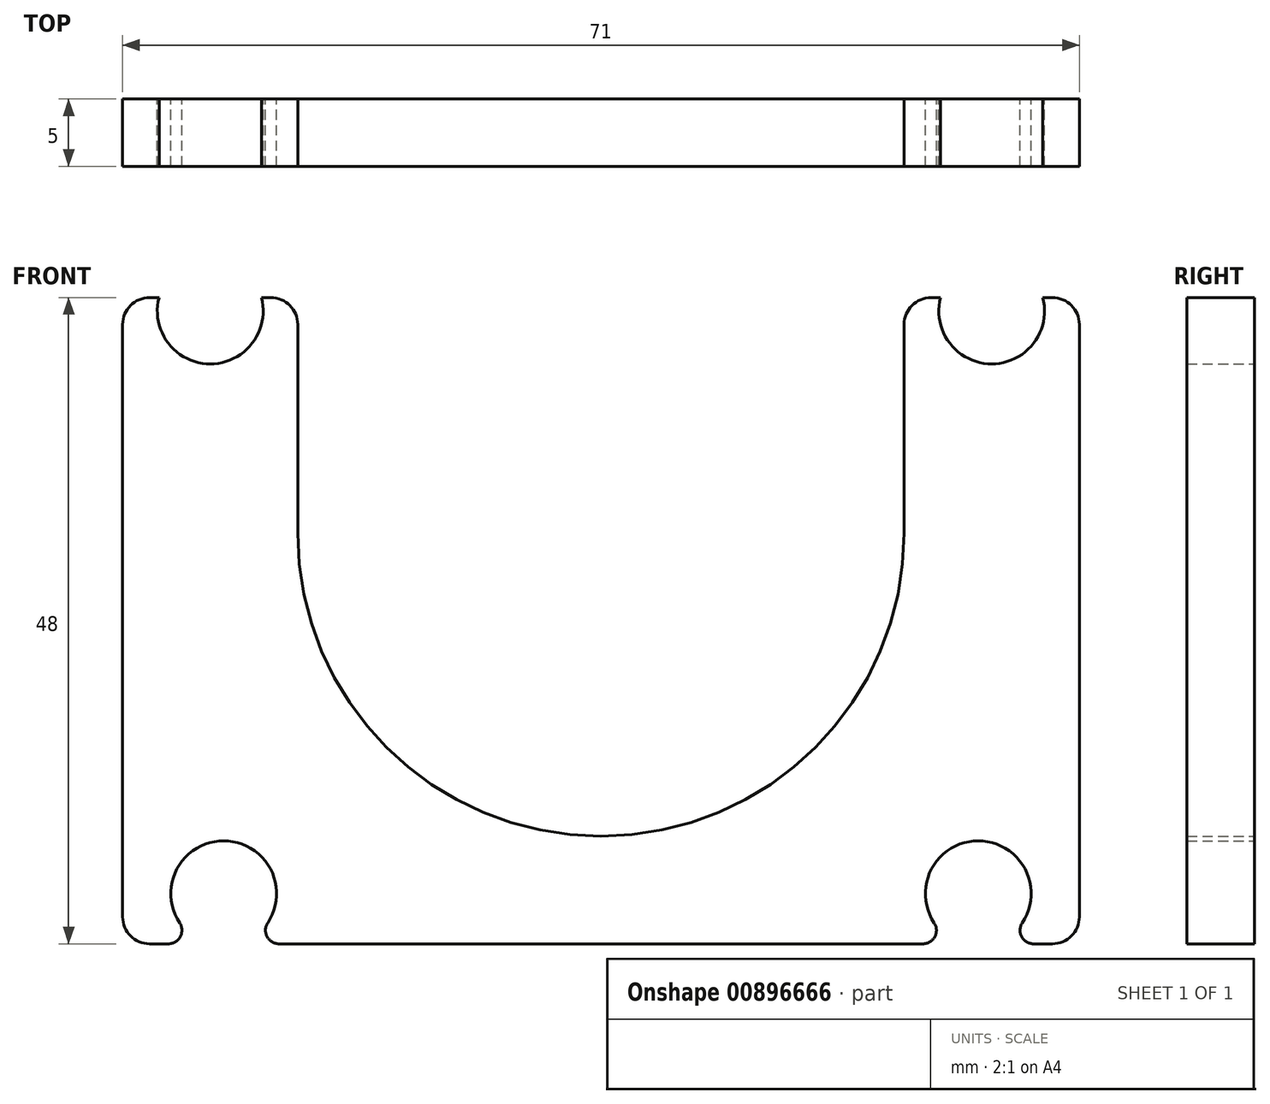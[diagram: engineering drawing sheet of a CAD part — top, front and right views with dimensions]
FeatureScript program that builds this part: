
annotation { "Feature Type Name" : "Feature", "Feature Type Description" : "" }
export const myFeature = defineFeature(function(context is Context, id is Id, definition is map)
    precondition{}
    {
        {
            var Q0;
            Q0=qCreatedBy(makeId("Front.planeOp"),FACE);
            var sketch = newSketch(context, id + "F0", { "sketchPlane" : qUnion([Q0])});
            skArc(sketch, "E0", {"start": v(-22.5, 30.5) * mm, "mid": v(0, 8) * mm, "end": v(22.5, 30.5) * mm});
            skLineSegment(sketch, "E1.bottom", {"start": v(-35.5, 48) * mm, "end": v(-32.8, 48) * mm});
            skLineSegment(sketch, "E1.top", {"start": v(-35.5, 0) * mm, "end": v(35.5, 0) * mm});
            skLineSegment(sketch, "E1.left", {"start": v(-35.5, 48) * mm, "end": v(-35.5, 0) * mm});
            skLineSegment(sketch, "E1.right", {"start": v(35.5, 48) * mm, "end": v(35.5, 0) * mm});
            skPoint(sketch, "E2", {"position": v(0, 0) * mm});
            skLineSegment(sketch, "E3", {"start": v(-22.5, 30.5) * mm, "end": v(-22.5, 48) * mm});
            skLineSegment(sketch, "E4.MirrorCS", {"start": v(22.5, 30.5) * mm, "end": v(22.5, 48) * mm});
            skLineSegment(sketch, "E5.trimOffspring", {"start": v(22.5, 48) * mm, "end": v(25.2, 48) * mm});
            skArc(sketch, "E6", {"start": v(25.2, 48) * mm, "mid": v(29, 43.08) * mm, "end": v(32.8, 48) * mm});
            skPoint(sketch, "E6.centerSnap0", {"position": v(29, 48) * mm});
            skLineSegment(sketch, "E7.trimOffspring", {"start": v(32.8, 48) * mm, "end": v(35.5, 48) * mm});
            skArc(sketch, "E8.MirrorCS", {"start": v(-25.2, 48) * mm, "mid": v(-29, 43.08) * mm, "end": v(-32.8, 48) * mm});
            skLineSegment(sketch, "E9.trimOffspring", {"start": v(-25.2, 48) * mm, "end": v(-22.5, 48) * mm});
            skSolve(sketch);
        }
        {
            var Q0;
            Q0=qSketchRegion(id+"F0",true);
            extrude(context, id + "F1", {"entities" : qUnion([Q0]), "depth" : 5 * mm, "offsetDistance" : 25 * mm});
        }
        {
            var Q0;
            Q0=qCreatedBy(makeId("Front.planeOp"),FACE);
            var sketch = newSketch(context, id + "F2", { "sketchPlane" : qUnion([Q0])});
            skCircle(sketch, "E10", {"center": v(-28, 3.72) * mm, "radius": 3.92 * mm});
            skCircle(sketch, "E11.MirrorC", {"center": v(28, 3.72) * mm, "radius": 3.92 * mm});
            skSolve(sketch);
        }
        {
            var Q0;
            Q0=qSketchRegion(id+"F2",true);
            extrude(context, id + "F3", {"entities" : qUnion([Q0]), "operationType" : NewBodyOperationType.REMOVE, "endBound" : BoundingType.THROUGH_ALL, "depth" : 25 * mm, "offsetDistance" : 25 * mm});
        }
        {
            var Q0;
            Q0=makeQuery(id+"F1.opExtrude","SWEPT_EDGE",EDGE,{"disambiguationData":[OSD([sQuery(id+"F0.wireOp",EDGE,"E3"),sQuery(id+"F0.wireOp",EDGE,"E9.trimOffspring")])]});
            var Q1;
            Q1=makeQuery(id+"F1.opExtrude","SWEPT_EDGE",EDGE,{"disambiguationData":[OSD([sQuery(id+"F0.wireOp",EDGE,"E4.MirrorCS"),sQuery(id+"F0.wireOp",EDGE,"E5.trimOffspring")])]});
            var Q2;
            Q2=makeQuery(id+"F1.opExtrude","SWEPT_EDGE",EDGE,{"disambiguationData":[OSD([sQuery(id+"F0.wireOp",EDGE,"E1.bottom"),sQuery(id+"F0.wireOp",EDGE,"E1.left")])]});
            var Q3;
            Q3=makeQuery(id+"F1.opExtrude","SWEPT_EDGE",EDGE,{"disambiguationData":[OSD([sQuery(id+"F0.wireOp",EDGE,"E1.right"),sQuery(id+"F0.wireOp",EDGE,"E7.trimOffspring")])]});
            var Q4;
            Q4=makeQuery(id+"F1.opExtrude","SWEPT_EDGE",EDGE,{"disambiguationData":[OSD([sQuery(id+"F0.wireOp",EDGE,"E1.top"),sQuery(id+"F0.wireOp",EDGE,"E1.right")])]});
            var Q5;
            Q5=makeQuery(id+"F1.opExtrude","SWEPT_EDGE",EDGE,{"disambiguationData":[OSD([sQuery(id+"F0.wireOp",EDGE,"E1.top"),sQuery(id+"F0.wireOp",EDGE,"E1.left")])]});
            fillet(context, id + "F4", {"entities" : qUnion([Q0, Q1, Q2, Q3, Q4, Q5]), "radius" : 2 * mm, "tangentPropagation" : true, "allowEdgeOverflow" : false});
        }
        {
            var Q0;
            Q0=makeQuery(id+"F3.boolean.opBoolean","INTERSECT",EDGE,{"disambiguationData":[OD(1.0)],"derivedFrom":[makeQuery(id+"F1.opExtrude","SWEPT_FACE",FACE,{"disambiguationData":[OSD([sQuery(id+"F0.wireOp",EDGE,"E1.top")])]}),makeQuery(id+"F3.opExtrude","SWEPT_FACE",FACE,{"disambiguationData":[OSD([sQuery(id+"F2.wireOp",EDGE,"E10")])]})]});
            var Q1;
            Q1=makeQuery(id+"F3.boolean.opBoolean","INTERSECT",EDGE,{"disambiguationData":[OD(0.0)],"derivedFrom":[makeQuery(id+"F1.opExtrude","SWEPT_FACE",FACE,{"disambiguationData":[OSD([sQuery(id+"F0.wireOp",EDGE,"E1.top")])]}),makeQuery(id+"F3.opExtrude","SWEPT_FACE",FACE,{"disambiguationData":[OSD([sQuery(id+"F2.wireOp",EDGE,"E10")])]})]});
            var Q2;
            Q2=makeQuery(id+"F3.boolean.opBoolean","INTERSECT",EDGE,{"disambiguationData":[OD(1.0)],"derivedFrom":[makeQuery(id+"F1.opExtrude","SWEPT_FACE",FACE,{"disambiguationData":[OSD([sQuery(id+"F0.wireOp",EDGE,"E1.top")])]}),makeQuery(id+"F3.opExtrude","SWEPT_FACE",FACE,{"disambiguationData":[OSD([sQuery(id+"F2.wireOp",EDGE,"E11.MirrorC")])]})]});
            var Q3;
            Q3=makeQuery(id+"F3.boolean.opBoolean","INTERSECT",EDGE,{"disambiguationData":[OD(0.0)],"derivedFrom":[makeQuery(id+"F1.opExtrude","SWEPT_FACE",FACE,{"disambiguationData":[OSD([sQuery(id+"F0.wireOp",EDGE,"E1.top")])]}),makeQuery(id+"F3.opExtrude","SWEPT_FACE",FACE,{"disambiguationData":[OSD([sQuery(id+"F2.wireOp",EDGE,"E11.MirrorC")])]})]});
            fillet(context, id + "F5", {"entities" : qUnion([Q0, Q1, Q2, Q3]), "radius" : 1 * mm, "tangentPropagation" : true, "allowEdgeOverflow" : false});
        }
    });
